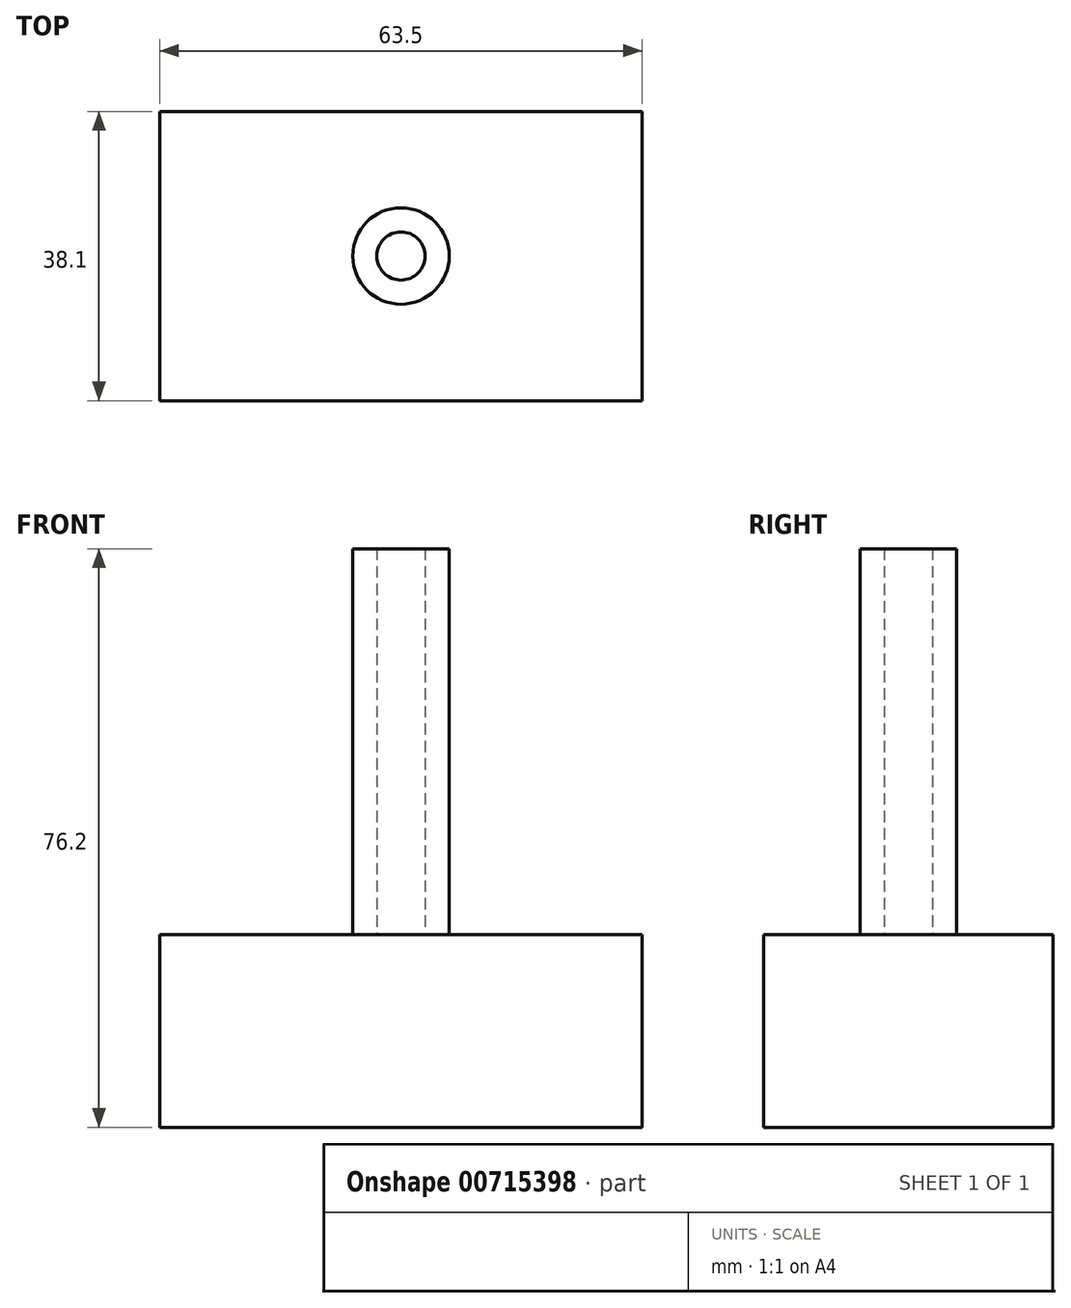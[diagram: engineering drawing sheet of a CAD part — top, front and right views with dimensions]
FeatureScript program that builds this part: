
annotation { "Feature Type Name" : "Feature", "Feature Type Description" : "" }
export const myFeature = defineFeature(function(context is Context, id is Id, definition is map)
    precondition{}
    {
        {
            var Q0;
            Q0=qCreatedBy(makeId("Top.planeOp"),FACE);
            var sketch = newSketch(context, id + "F0", { "sketchPlane" : qUnion([Q0])});
            skLineSegment(sketch, "E0.bottom", {"start": v(-57.32, 5.03) * mm, "end": v(6.18, 5.03) * mm});
            skLineSegment(sketch, "E0.top", {"start": v(-57.32, -33.07) * mm, "end": v(6.18, -33.07) * mm});
            skLineSegment(sketch, "E0.left", {"start": v(-57.32, 5.03) * mm, "end": v(-57.32, -33.07) * mm});
            skLineSegment(sketch, "E0.right", {"start": v(6.18, 5.03) * mm, "end": v(6.18, -33.07) * mm});
            skSolve(sketch);
        }
        {
            var Q0;
            Q0=makeQuery(id+"F0.imprint","IMPRINT",FACE,{"disambiguationData":[TD([[makeQuery(id+"F0.imprint","IMPRINT",EDGE,{"derivedFrom":sQuery(id+"F0.wireOp",EDGE,"E0.bottom")}),-1.0]])]});
            extrude(context, id + "F1", {"entities" : qUnion([Q0]), "depth" : 25.4 * mm, "offsetDistance" : 25.4 * mm});
        }
        {
            var Q0;
            Q0=makeQuery(id+"F1.opExtrude","CAP_FACE",FACE,{"disambiguationData":[OSD([sQuery(id+"F0.wireOp",EDGE,"E0.bottom"),sQuery(id+"F0.wireOp",EDGE,"E0.top"),sQuery(id+"F0.wireOp",EDGE,"E0.left"),sQuery(id+"F0.wireOp",EDGE,"E0.right")])],"isStart":false});
            var sketch = newSketch(context, id + "F2", { "sketchPlane" : qUnion([Q0])});
            skCircle(sketch, "E1", {"center": v(-25.57, -14.02) * mm, "radius": 3.18 * mm});
            skCircle(sketch, "E2", {"center": v(-25.57, -14.02) * mm, "radius": 6.35 * mm});
            skSolve(sketch);
        }
        {
            var Q0;
            Q0=makeQuery(id+"F2.imprint","IMPRINT",FACE,{"disambiguationData":[TD([[makeQuery(id+"F2.imprint","IMPRINT",EDGE,{"derivedFrom":sQuery(id+"F2.wireOp",EDGE,"E1")}),-1.0]])]});
            extrude(context, id + "F3", {"entities" : qUnion([Q0]), "operationType" : NewBodyOperationType.ADD, "depth" : 50.8 * mm, "offsetDistance" : 25.4 * mm});
        }
    });
